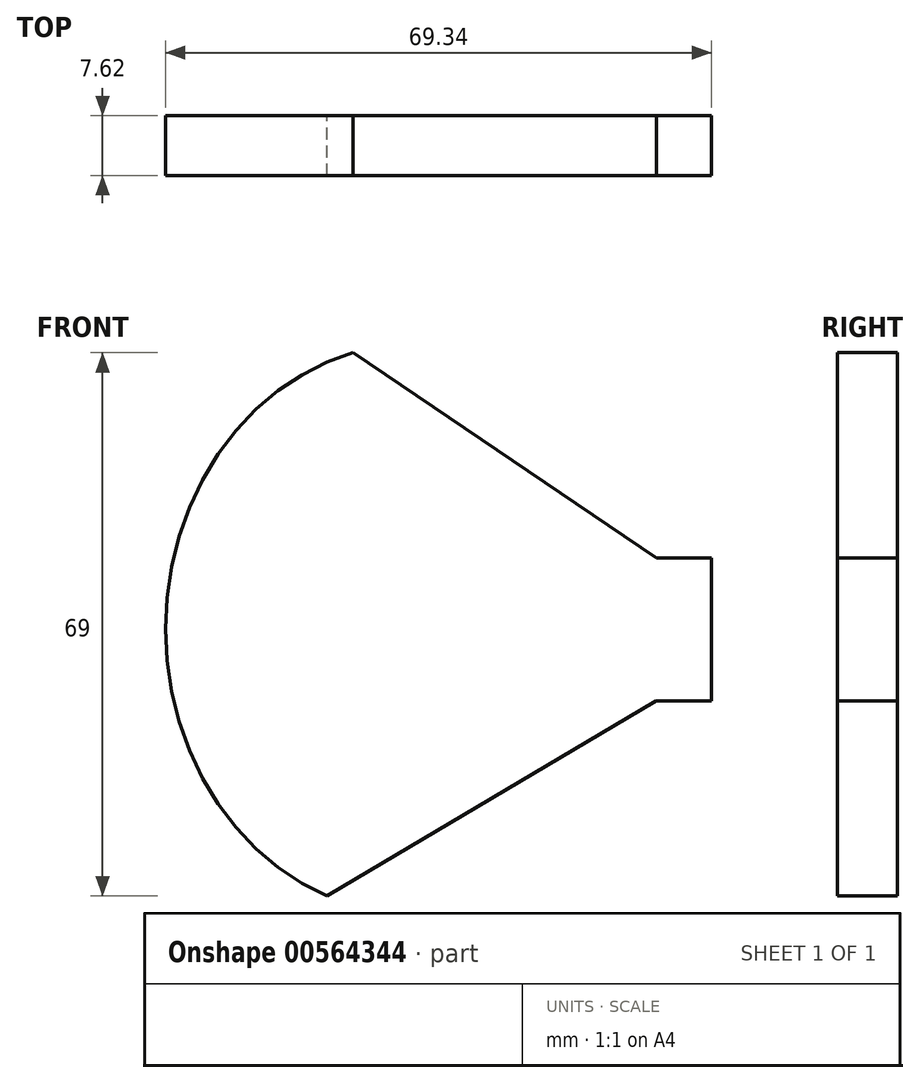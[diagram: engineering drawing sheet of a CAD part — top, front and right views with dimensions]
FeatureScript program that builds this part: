
annotation { "Feature Type Name" : "Feature", "Feature Type Description" : "" }
export const myFeature = defineFeature(function(context is Context, id is Id, definition is map)
    precondition{}
    {
        {
            var Q0;
            Q0=qCreatedBy(makeId("Front.planeOp"),FACE);
            var sketch = newSketch(context, id + "F0", { "sketchPlane" : qUnion([Q0])});
            skPoint(sketch, "E0.end.orphan", {"position": v(25.42, -10.19) * mm});
            skPoint(sketch, "E1.center.orphan", {"position": v(25.42, -16.49) * mm});
            skPoint(sketch, "E2.centerSnap0", {"position": v(27.96, -16.2) * mm});
            skPoint(sketch, "E3.orphan", {"position": v(22.68, -10.16) * mm});
            skEllipticalArc(sketch, "E4", {});
            skPoint(sketch, "E5.start.orphan", {"position": v(27.96, -22.25) * mm});
            skPoint(sketch, "E6.end.orphan", {"position": v(27.96, -10.16) * mm});
            skLineSegment(sketch, "E7.bottom", {"start": v(47, -7.45) * mm, "end": v(40, -7.45) * mm});
            skLineSegment(sketch, "E7.top", {"start": v(47, -25.65) * mm, "end": v(39.97, -25.65) * mm});
            skLineSegment(sketch, "E7.left", {"start": v(47, -7.45) * mm, "end": v(47, -25.65) * mm});
            skLineSegment(sketch, "E8", {"start": v(40, -7.45) * mm, "end": v(1.48, 18.6) * mm});
            skLineSegment(sketch, "E9", {"start": v(39.97, -25.65) * mm, "end": v(-1.83, -50.39) * mm});
            const initialGuessF0  = {"E4": [0.009324885904788971, -0.016487352685956594, 0, -1, 0.036222372068138484, 0.03167699983413693, 3.3919385934648942, 5.923226367610577]};
            skSetInitialGuess(sketch, initialGuessF0);
            skSolve(sketch);
        }
        {
            var Q0;
            Q0 = qSketchRegion(id + "F0", true);
            extrude(context, id + "F1", {"entities" : qUnion([Q0]), "depth" : 7.62 * mm, "offsetDistance" : 25.4 * mm, "symmetric" : true});
        }
    });
